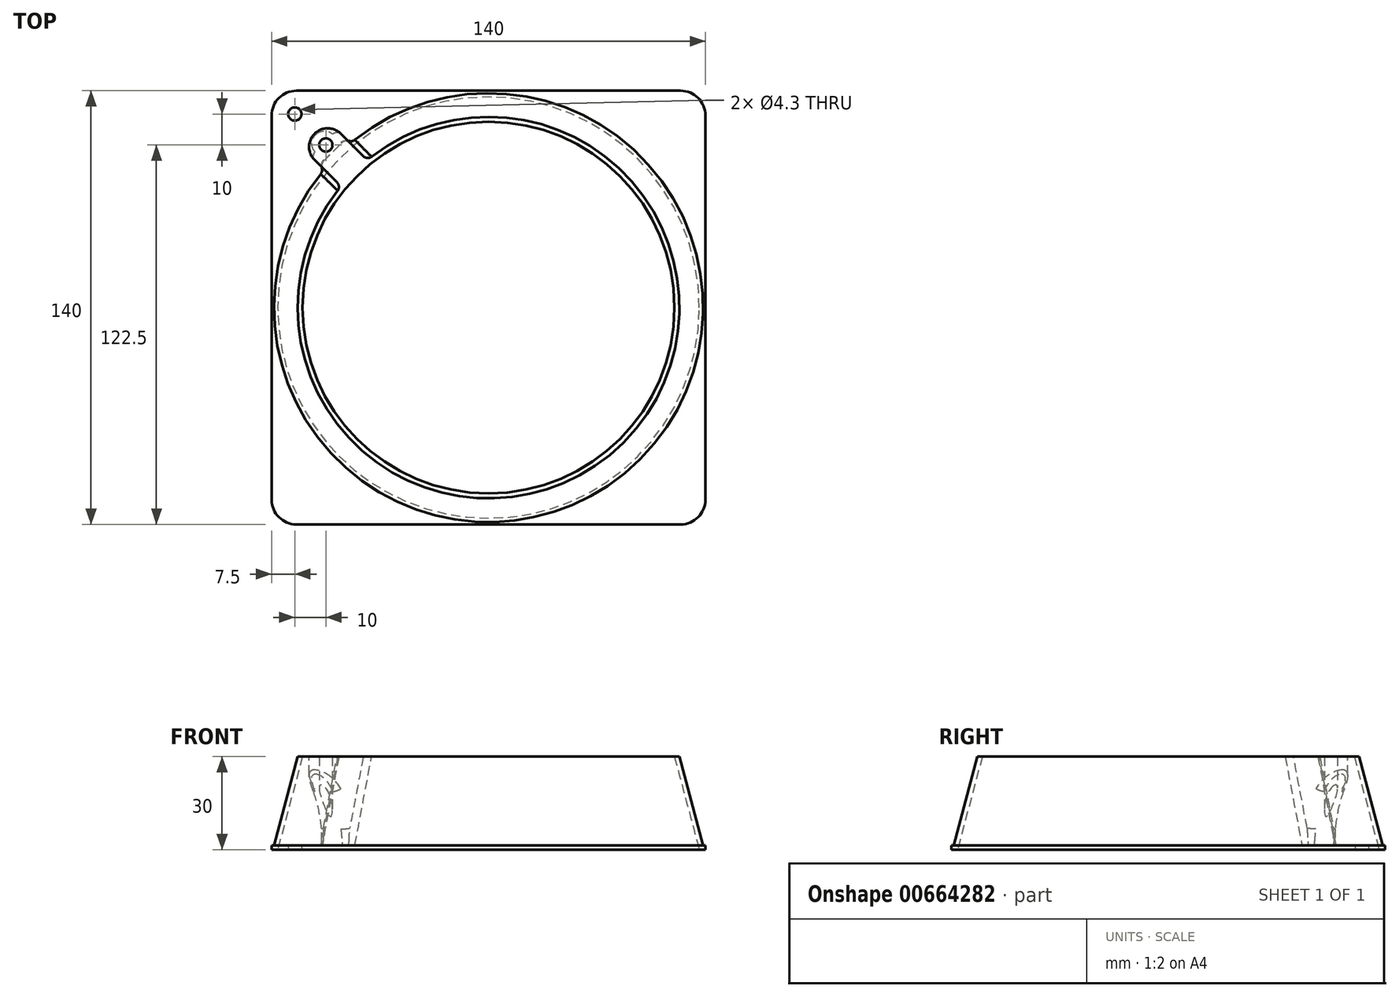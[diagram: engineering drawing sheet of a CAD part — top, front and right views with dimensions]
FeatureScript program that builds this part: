
annotation { "Feature Type Name" : "Feature", "Feature Type Description" : "" }
export const myFeature = defineFeature(function(context is Context, id is Id, definition is map)
    precondition{}
    {
        {
            var Q0;
            Q0=qCreatedBy(makeId("Top.planeOp"),FACE);
            var sketch = newSketch(context, id + "F0", { "sketchPlane" : qUnion([Q0])});
            skLineSegment(sketch, "E0.bottom", {"start": v(-70, 70) * mm, "end": v(70, 70) * mm});
            skLineSegment(sketch, "E0.top", {"start": v(-70, -70) * mm, "end": v(70, -70) * mm});
            skLineSegment(sketch, "E0.left", {"start": v(-70, 70) * mm, "end": v(-70, -70) * mm});
            skLineSegment(sketch, "E0.right", {"start": v(70, 70) * mm, "end": v(70, -70) * mm});
            skSolve(sketch);
        }
        {
            var Q0;
            Q0 = qSketchRegion(id + "F0", true);
            extrude(context, id + "F1", {"entities" : qUnion([Q0]), "depth" : 30 * mm, "offsetDistance" : 25 * mm});
        }
        {
            var Q0;
            Q0=qCreatedBy(makeId("Top.planeOp"),FACE);
            var sketch = newSketch(context, id + "F2", { "sketchPlane" : qUnion([Q0])});
            skCircle(sketch, "E1", {"center": v(-62.5, 62.5) * mm, "radius": 2.15 * mm});
            skSolve(sketch);
        }
        {
            var Q0;
            Q0=qCreatedBy(makeId("Right.planeOp"),FACE);
            var sketch = newSketch(context, id + "F3", { "sketchPlane" : qUnion([Q0])});
            skLineSegment(sketch, "E2", {"start": v(0, -23.45) * mm, "end": v(0, 54.65) * mm, "construction": true});
            skSolve(sketch);
        }
        {
            var Q0;
            Q0=qCreatedBy(makeId("Top.planeOp"),FACE);
            var sketch = newSketch(context, id + "F4", { "sketchPlane" : qUnion([Q0])});
            skCircle(sketch, "E3", {"center": v(0, 0) * mm, "radius": 68 * mm});
            skSolve(sketch);
        }
        {
            var Q0;
            Q0=makeQuery(id+"F0.imprint","IMPRINT",FACE,{"disambiguationData":[TD([[makeQuery(id+"F0.imprint","IMPRINT",EDGE,{"derivedFrom":sQuery(id+"F0.wireOp",EDGE,"E0.bottom")}),-1.0]])]});
            var sketch = newSketch(context, id + "F5", { "sketchPlane" : qUnion([Q0])});
            skCircle(sketch, "E4", {"center": v(0, 0) * mm, "radius": 69.6 * mm});
            skLineSegment(sketch, "E5.bottom", {"start": v(-83.67, 77.05) * mm, "end": v(82.18, 77.05) * mm});
            skLineSegment(sketch, "E5.top", {"start": v(-83.67, -76.06) * mm, "end": v(82.18, -76.06) * mm});
            skLineSegment(sketch, "E5.left", {"start": v(-83.67, 77.05) * mm, "end": v(-83.67, -76.06) * mm});
            skLineSegment(sketch, "E5.right", {"start": v(82.18, 77.05) * mm, "end": v(82.18, -76.06) * mm});
            skSolve(sketch);
        }
        {
            var Q0;
            Q0 = qSketchRegion(id + "F5", true);
            extrude(context, id + "F6", {"entities" : qUnion([Q0]), "operationType" : NewBodyOperationType.REMOVE, "depth" : 30 * mm, "offsetDistance" : 25 * mm, "hasDraft" : true, "draftAngle" : 14.93 * degree, "hasSecondDirection" : true, "secondDirectionOppositeDirection" : false, "secondDirectionDepth" : 1.4 * mm});
        }
        {
            var Q0;
            Q0=qCreatedBy(makeId("Top.planeOp"),FACE);
            var sketch = newSketch(context, id + "F7", { "sketchPlane" : qUnion([Q0])});
            skCircle(sketch, "E6", {"center": v(-52.5, 52.5) * mm, "radius": 2.15 * mm});
            skSolve(sketch);
        }
        {
            var Q0;
            Q0=makeQuery(id+"F0.imprint","IMPRINT",FACE,{"disambiguationData":[TD([[makeQuery(id+"F0.imprint","IMPRINT",EDGE,{"derivedFrom":sQuery(id+"F0.wireOp",EDGE,"E0.bottom")}),-1.0]])]});
            var sketch = newSketch(context, id + "F8", { "sketchPlane" : qUnion([Q0])});
            skLineSegment(sketch, "E7", {"start": v(-45.5, 37.02) * mm, "end": v(-37.02, 45.5) * mm});
            skLineSegment(sketch, "E8", {"start": v(0, 0) * mm, "end": v(-70, 70) * mm, "construction": true});
            skLineSegment(sketch, "E9", {"start": v(-45.5, 37.02) * mm, "end": v(-60.38, 51.9) * mm});
            skLineSegment(sketch, "E10", {"start": v(-37.02, 45.5) * mm, "end": v(-51.9, 60.38) * mm});
            skLineSegment(sketch, "E11", {"start": v(-60.38, 51.9) * mm, "end": v(-51.9, 60.38) * mm});
            skSolve(sketch);
        }
        {
            var Q0;
            Q0 = qSketchRegion(id + "F8", true);
            extrude(context, id + "F9", {"entities" : qUnion([Q0]), "operationType" : NewBodyOperationType.ADD, "depth" : 30 * mm, "offsetDistance" : 25 * mm});
        }
        {
            var Q0;
            Q0 = qSketchRegion(id + "F2", true);
            extrude(context, id + "F10", {"entities" : qUnion([Q0]), "operationType" : NewBodyOperationType.REMOVE, "depth" : 5 * mm, "offsetDistance" : 25 * mm});
        }
        {
            var Q0;
            Q0 = qSketchRegion(id + "F4", true);
            extrude(context, id + "F11", {"entities" : qUnion([Q0]), "operationType" : NewBodyOperationType.REMOVE, "depth" : 30 * mm, "offsetDistance" : 25 * mm, "hasDraft" : true, "draftAngle" : 14.93 * degree, "draftPullDirection" : true});
        }
        {
            var Q0;
            Q0=makeQuery(id+"F9.boolean.opBoolean","MERGE",EDGE,{"derivedFrom":[makeQuery(id+"F1.opExtrude","SWEPT_EDGE",EDGE,{"disambiguationData":[OSD([sQuery(id+"F0.wireOp",EDGE,"E0.bottom"),sQuery(id+"F0.wireOp",EDGE,"E0.left")])]}),makeQuery(id+"F9.opExtrude","SWEPT_EDGE",EDGE,{"disambiguationData":[OSD([sQuery(id+"F8.wireOp",EDGE,"bcqxiliO-g36q-Js58-HRms-isVHzeuhr4qR"),sQuery(id+"F8.wireOp",EDGE,"sepJio0f-Bdl7-0CLp-PTzf-5zJ3YjW6fdva")])]})]});
            var Q1;
            Q1=makeQuery(id+"FmQ22TMhTTGu5hA_1.3.F9.boolean.opBoolean","MERGE",EDGE,{"derivedFrom":[makeQuery(id+"F1.opExtrude","SWEPT_EDGE",EDGE,{"disambiguationData":[OSD([sQuery(id+"F0.wireOp",EDGE,"E0.bottom"),sQuery(id+"F0.wireOp",EDGE,"E0.right")])]}),makeQuery(id+"FmQ22TMhTTGu5hA_1.3.F9.opExtrude","SWEPT_EDGE",EDGE,{"disambiguationData":[OSD([sQuery(id+"F8.wireOp",EDGE,"bcqxiliO-g36q-Js58-HRms-isVHzeuhr4qR"),sQuery(id+"F8.wireOp",EDGE,"sepJio0f-Bdl7-0CLp-PTzf-5zJ3YjW6fdva")])]})]});
            var Q2;
            Q2=makeQuery(id+"FmQ22TMhTTGu5hA_1.2.F9.boolean.opBoolean","MERGE",EDGE,{"derivedFrom":[makeQuery(id+"F1.opExtrude","SWEPT_EDGE",EDGE,{"disambiguationData":[OSD([sQuery(id+"F0.wireOp",EDGE,"E0.top"),sQuery(id+"F0.wireOp",EDGE,"E0.right")])]}),makeQuery(id+"FmQ22TMhTTGu5hA_1.2.F9.opExtrude","SWEPT_EDGE",EDGE,{"disambiguationData":[OSD([sQuery(id+"F8.wireOp",EDGE,"bcqxiliO-g36q-Js58-HRms-isVHzeuhr4qR"),sQuery(id+"F8.wireOp",EDGE,"sepJio0f-Bdl7-0CLp-PTzf-5zJ3YjW6fdva")])]})]});
            var Q3;
            Q3=makeQuery(id+"FmQ22TMhTTGu5hA_1.1.F9.boolean.opBoolean","MERGE",EDGE,{"derivedFrom":[makeQuery(id+"F1.opExtrude","SWEPT_EDGE",EDGE,{"disambiguationData":[OSD([sQuery(id+"F0.wireOp",EDGE,"E0.top"),sQuery(id+"F0.wireOp",EDGE,"E0.left")])]}),makeQuery(id+"FmQ22TMhTTGu5hA_1.1.F9.opExtrude","SWEPT_EDGE",EDGE,{"disambiguationData":[OSD([sQuery(id+"F8.wireOp",EDGE,"bcqxiliO-g36q-Js58-HRms-isVHzeuhr4qR"),sQuery(id+"F8.wireOp",EDGE,"sepJio0f-Bdl7-0CLp-PTzf-5zJ3YjW6fdva")])]})]});
            fillet(context, id + "F12", {"entities" : qUnion([Q0, Q1, Q2, Q3]), "radius" : 8 * mm, "tangentPropagation" : true, "allowEdgeOverflow" : false});
        }
        {
            var Q0;
            Q0 = qSketchRegion(id + "F7", true);
            extrude(context, id + "F13", {"entities" : qUnion([Q0]), "operationType" : NewBodyOperationType.REMOVE, "depth" : 30 * mm, "offsetDistance" : 25 * mm, "hasSecondDirection" : true, "secondDirectionOppositeDirection" : false, "secondDirectionDepth" : 10 * mm});
        }
        {
            var Q0;
            Q0=qCreatedBy(makeId("Top.planeOp"),FACE);
            var sketch = newSketch(context, id + "F14", { "sketchPlane" : qUnion([Q0])});
            skLineSegment(sketch, "E12", {"start": v(-54.87, 45.68) * mm, "end": v(-62.15, 52.96) * mm});
            skLineSegment(sketch, "E13", {"start": v(-62.15, 52.96) * mm, "end": v(-52.96, 62.15) * mm});
            skLineSegment(sketch, "E14", {"start": v(-52.96, 62.15) * mm, "end": v(-45.68, 54.87) * mm});
            skLineSegment(sketch, "E15", {"start": v(-54.87, 45.68) * mm, "end": v(-45.68, 54.87) * mm});
            skSolve(sketch);
        }
        {
            var Q0;
            Q0 = qSketchRegion(id + "F14", true);
            extrude(context, id + "F15", {"entities" : qUnion([Q0]), "operationType" : NewBodyOperationType.REMOVE, "depth" : 25 * mm, "offsetDistance" : 25 * mm, "hasSecondDirection" : true, "secondDirectionOppositeDirection" : false, "secondDirectionDepth" : 1.4 * mm});
        }
        {
            var Q0;
            Q0=makeQuery(id+"FmQ22TMhTTGu5hA_1.1.F9.boolean.opBoolean","INTERSECT",EDGE,{"derivedFrom":[makeQuery(id+"F6.boolean.opBoolean","COPY",FACE,{"derivedFrom":makeQuery(id+"F6.opExtrude","SWEPT_FACE",FACE,{"disambiguationData":[OSD([sQuery(id+"F5.wireOp",EDGE,"E4")])]})}),makeQuery(id+"FmQ22TMhTTGu5hA_1.1.F9.opExtrude","SWEPT_FACE",FACE,{"disambiguationData":[OSD([sQuery(id+"F8.wireOp",EDGE,"E9")])]})]});
            var Q1;
            Q1=makeQuery(id+"FmQ22TMhTTGu5hA_1.1.F9.boolean.opBoolean","INTERSECT",EDGE,{"derivedFrom":[makeQuery(id+"F6.boolean.opBoolean","COPY",FACE,{"derivedFrom":makeQuery(id+"F6.opExtrude","SWEPT_FACE",FACE,{"disambiguationData":[OSD([sQuery(id+"F5.wireOp",EDGE,"E4")])]})}),makeQuery(id+"FmQ22TMhTTGu5hA_1.1.F9.opExtrude","SWEPT_FACE",FACE,{"disambiguationData":[OSD([sQuery(id+"F8.wireOp",EDGE,"E10")])]})]});
            var Q2;
            {var subQ0=sQuery(id+"F8.wireOp",EDGE,"E10");var subQ4=sQuery(id+"F5.wireOp",EDGE,"E4");Q2=makeQuery(id+"FmQ22TMhTTGu5hA_1.2.F9.boolean.opBoolean","INTERSECT",EDGE,{"derivedFrom":[makeQuery(id+"FmQ22TMhTTGu5hA_1.1.F9.boolean.opBoolean","SPLIT",FACE,{"disambiguationData":[TD([makeQuery(id+"F9.opExtrude","SWEPT_FACE",FACE,{"disambiguationData":[OSD([subQ0])]})])],"derivedFrom":makeQuery(id+"F6.boolean.opBoolean","COPY",FACE,{"derivedFrom":makeQuery(id+"F6.opExtrude","SWEPT_FACE",FACE,{"disambiguationData":[OSD([subQ4])]})})}),makeQuery(id+"FmQ22TMhTTGu5hA_1.2.F9.opExtrude","SWEPT_FACE",FACE,{"disambiguationData":[OSD([subQ0])]})]});}
            var Q3;
            {var subQ0=sQuery(id+"F8.wireOp",EDGE,"E9");var subQ1=sQuery(id+"F8.wireOp",EDGE,"E10");var subQ4=sQuery(id+"F5.wireOp",EDGE,"E4");Q3=makeQuery(id+"FmQ22TMhTTGu5hA_1.2.F9.boolean.opBoolean","INTERSECT",EDGE,{"derivedFrom":[makeQuery(id+"FmQ22TMhTTGu5hA_1.1.F9.boolean.opBoolean","SPLIT",FACE,{"disambiguationData":[TD([makeQuery(id+"F9.opExtrude","SWEPT_FACE",FACE,{"disambiguationData":[OSD([subQ1])]})])],"derivedFrom":makeQuery(id+"F6.boolean.opBoolean","COPY",FACE,{"derivedFrom":makeQuery(id+"F6.opExtrude","SWEPT_FACE",FACE,{"disambiguationData":[OSD([subQ4])]})})}),makeQuery(id+"FmQ22TMhTTGu5hA_1.2.F9.opExtrude","SWEPT_FACE",FACE,{"disambiguationData":[OSD([subQ0])]})]});}
            var Q4;
            {var subQ0=sQuery(id+"F8.wireOp",EDGE,"E10");var subQ1=makeQuery(id+"F9.opExtrude","SWEPT_FACE",FACE,{"disambiguationData":[OSD([subQ0])]});var subQ6=sQuery(id+"F5.wireOp",EDGE,"E4");Q4=makeQuery(id+"FmQ22TMhTTGu5hA_1.3.F9.boolean.opBoolean","INTERSECT",EDGE,{"derivedFrom":[makeQuery(id+"FmQ22TMhTTGu5hA_1.2.F9.boolean.opBoolean","SPLIT",FACE,{"disambiguationData":[TD([subQ1])],"derivedFrom":makeQuery(id+"FmQ22TMhTTGu5hA_1.1.F9.boolean.opBoolean","SPLIT",FACE,{"disambiguationData":[TD([subQ1])],"derivedFrom":makeQuery(id+"F6.boolean.opBoolean","COPY",FACE,{"derivedFrom":makeQuery(id+"F6.opExtrude","SWEPT_FACE",FACE,{"disambiguationData":[OSD([subQ6])]})})})}),makeQuery(id+"FmQ22TMhTTGu5hA_1.3.F9.opExtrude","SWEPT_FACE",FACE,{"disambiguationData":[OSD([subQ0])]})]});}
            var Q5;
            {var subQ0=sQuery(id+"F8.wireOp",EDGE,"E9");var subQ1=sQuery(id+"F8.wireOp",EDGE,"E10");var subQ2=makeQuery(id+"F9.opExtrude","SWEPT_FACE",FACE,{"disambiguationData":[OSD([subQ1])]});var subQ6=sQuery(id+"F5.wireOp",EDGE,"E4");Q5=makeQuery(id+"FmQ22TMhTTGu5hA_1.3.F9.boolean.opBoolean","INTERSECT",EDGE,{"derivedFrom":[makeQuery(id+"FmQ22TMhTTGu5hA_1.2.F9.boolean.opBoolean","SPLIT",FACE,{"disambiguationData":[TD([subQ2])],"derivedFrom":makeQuery(id+"FmQ22TMhTTGu5hA_1.1.F9.boolean.opBoolean","SPLIT",FACE,{"disambiguationData":[TD([subQ2])],"derivedFrom":makeQuery(id+"F6.boolean.opBoolean","COPY",FACE,{"derivedFrom":makeQuery(id+"F6.opExtrude","SWEPT_FACE",FACE,{"disambiguationData":[OSD([subQ6])]})})})}),makeQuery(id+"FmQ22TMhTTGu5hA_1.3.F9.opExtrude","SWEPT_FACE",FACE,{"disambiguationData":[OSD([subQ0])]})]});}
            var Q6;
            Q6=makeQuery(id+"F9.boolean.opBoolean","INTERSECT",EDGE,{"derivedFrom":[makeQuery(id+"F6.boolean.opBoolean","COPY",FACE,{"derivedFrom":makeQuery(id+"F6.opExtrude","SWEPT_FACE",FACE,{"disambiguationData":[OSD([sQuery(id+"F5.wireOp",EDGE,"E4")])]})}),makeQuery(id+"F9.opExtrude","SWEPT_FACE",FACE,{"disambiguationData":[OSD([sQuery(id+"F8.wireOp",EDGE,"E10")])]})]});
            var Q7;
            Q7=makeQuery(id+"F9.boolean.opBoolean","INTERSECT",EDGE,{"derivedFrom":[makeQuery(id+"F6.boolean.opBoolean","COPY",FACE,{"derivedFrom":makeQuery(id+"F6.opExtrude","SWEPT_FACE",FACE,{"disambiguationData":[OSD([sQuery(id+"F5.wireOp",EDGE,"E4")])]})}),makeQuery(id+"F9.opExtrude","SWEPT_FACE",FACE,{"disambiguationData":[OSD([sQuery(id+"F8.wireOp",EDGE,"E9")])]})]});
            fillet(context, id + "F16", {"entities" : qUnion([Q0, Q1, Q2, Q3, Q4, Q5, Q6, Q7]), "radius" : 2 * mm, "tangentPropagation" : true, "allowEdgeOverflow" : false});
        }
        {
            var Q0;
            Q0=makeQuery(id+"FRqQuWRhVaArxQi_1.1.F15.boolean.opBoolean","COPY",EDGE,{"derivedFrom":makeQuery(id+"FRqQuWRhVaArxQi_1.1.F15.opExtrude","CAP_EDGE",EDGE,{"disambiguationData":[OSD([sQuery(id+"F14.wireOp",EDGE,"E15")])],"isStart":false})});
            var Q1;
            Q1=makeQuery(id+"FRqQuWRhVaArxQi_1.2.F15.boolean.opBoolean","COPY",EDGE,{"derivedFrom":makeQuery(id+"FRqQuWRhVaArxQi_1.2.F15.opExtrude","CAP_EDGE",EDGE,{"disambiguationData":[OSD([sQuery(id+"F14.wireOp",EDGE,"E15")])],"isStart":false})});
            var Q2;
            Q2=makeQuery(id+"FRqQuWRhVaArxQi_1.3.F15.boolean.opBoolean","COPY",EDGE,{"derivedFrom":makeQuery(id+"FRqQuWRhVaArxQi_1.3.F15.opExtrude","CAP_EDGE",EDGE,{"disambiguationData":[OSD([sQuery(id+"F14.wireOp",EDGE,"E15")])],"isStart":false})});
            var Q3;
            Q3=makeQuery(id+"F15.boolean.opBoolean","COPY",EDGE,{"derivedFrom":makeQuery(id+"F15.opExtrude","CAP_EDGE",EDGE,{"disambiguationData":[OSD([sQuery(id+"F14.wireOp",EDGE,"E15")])],"isStart":false})});
            fillet(context, id + "F17", {"entities" : qUnion([Q0, Q1, Q2, Q3]), "radius" : 35 * mm, "tangentPropagation" : true, "allowEdgeOverflow" : false});
        }
        {
            var Q0;
            Q0=makeQuery(id+"FmQ22TMhTTGu5hA_1.2.F9.opExtrude","SWEPT_EDGE",EDGE,{"disambiguationData":[OSD([sQuery(id+"F8.wireOp",EDGE,"E9"),sQuery(id+"F8.wireOp",EDGE,"E11")])]});
            var Q1;
            Q1=makeQuery(id+"FmQ22TMhTTGu5hA_1.3.F9.opExtrude","SWEPT_EDGE",EDGE,{"disambiguationData":[OSD([sQuery(id+"F8.wireOp",EDGE,"E10"),sQuery(id+"F8.wireOp",EDGE,"E11")])]});
            var Q2;
            Q2=makeQuery(id+"FmQ22TMhTTGu5hA_1.3.F9.opExtrude","SWEPT_EDGE",EDGE,{"disambiguationData":[OSD([sQuery(id+"F8.wireOp",EDGE,"E9"),sQuery(id+"F8.wireOp",EDGE,"E11")])]});
            var Q3;
            Q3=makeQuery(id+"F9.opExtrude","SWEPT_EDGE",EDGE,{"disambiguationData":[OSD([sQuery(id+"F8.wireOp",EDGE,"E10"),sQuery(id+"F8.wireOp",EDGE,"E11")])]});
            var Q4;
            Q4=makeQuery(id+"FmQ22TMhTTGu5hA_1.2.F9.opExtrude","SWEPT_EDGE",EDGE,{"disambiguationData":[OSD([sQuery(id+"F8.wireOp",EDGE,"E10"),sQuery(id+"F8.wireOp",EDGE,"E11")])]});
            var Q5;
            Q5=makeQuery(id+"FmQ22TMhTTGu5hA_1.1.F9.opExtrude","SWEPT_EDGE",EDGE,{"disambiguationData":[OSD([sQuery(id+"F8.wireOp",EDGE,"E9"),sQuery(id+"F8.wireOp",EDGE,"E11")])]});
            var Q6;
            Q6=makeQuery(id+"FmQ22TMhTTGu5hA_1.1.F9.opExtrude","SWEPT_EDGE",EDGE,{"disambiguationData":[OSD([sQuery(id+"F8.wireOp",EDGE,"E10"),sQuery(id+"F8.wireOp",EDGE,"E11")])]});
            var Q7;
            Q7=makeQuery(id+"F9.opExtrude","SWEPT_EDGE",EDGE,{"disambiguationData":[OSD([sQuery(id+"F8.wireOp",EDGE,"E9"),sQuery(id+"F8.wireOp",EDGE,"E11")])]});
            fillet(context, id + "F18", {"entities" : qUnion([Q0, Q1, Q2, Q3, Q4, Q5, Q6, Q7]), "radius" : 6 * mm, "tangentPropagation" : true, "allowEdgeOverflow" : false});
        }
        {
            var Q0;
            Q0=makeQuery(id+"F17.opFillet","BLEND_EDGE",EDGE,{"blendedFrom":[makeQuery(id+"FRqQuWRhVaArxQi_1.1.F15.boolean.opBoolean","COPY",EDGE,{"derivedFrom":makeQuery(id+"FRqQuWRhVaArxQi_1.1.F15.opExtrude","CAP_EDGE",EDGE,{"disambiguationData":[OSD([sQuery(id+"F14.wireOp",EDGE,"E15")])],"isStart":false})}),makeQuery(id+"FmQ22TMhTTGu5hA_1.1.F9.opExtrude","SWEPT_FACE",FACE,{"disambiguationData":[OSD([sQuery(id+"F8.wireOp",EDGE,"E9")])]})],"blendedInto":[makeQuery(id+"FmQ22TMhTTGu5hA_1.1.F9.opExtrude","SWEPT_FACE",FACE,{"disambiguationData":[OSD([sQuery(id+"F8.wireOp",EDGE,"E9")])]})]});
            var Q1;
            Q1=makeQuery(id+"F17.opFillet","BLEND_EDGE",EDGE,{"blendedFrom":[makeQuery(id+"FRqQuWRhVaArxQi_1.2.F15.boolean.opBoolean","COPY",EDGE,{"derivedFrom":makeQuery(id+"FRqQuWRhVaArxQi_1.2.F15.opExtrude","CAP_EDGE",EDGE,{"disambiguationData":[OSD([sQuery(id+"F14.wireOp",EDGE,"E15")])],"isStart":false})}),makeQuery(id+"FmQ22TMhTTGu5hA_1.2.F9.opExtrude","SWEPT_FACE",FACE,{"disambiguationData":[OSD([sQuery(id+"F8.wireOp",EDGE,"E9")])]})],"blendedInto":[makeQuery(id+"FmQ22TMhTTGu5hA_1.2.F9.opExtrude","SWEPT_FACE",FACE,{"disambiguationData":[OSD([sQuery(id+"F8.wireOp",EDGE,"E9")])]})]});
            var Q2;
            Q2=makeQuery(id+"F17.opFillet","BLEND_EDGE",EDGE,{"blendedFrom":[makeQuery(id+"FRqQuWRhVaArxQi_1.3.F15.boolean.opBoolean","COPY",EDGE,{"derivedFrom":makeQuery(id+"FRqQuWRhVaArxQi_1.3.F15.opExtrude","CAP_EDGE",EDGE,{"disambiguationData":[OSD([sQuery(id+"F14.wireOp",EDGE,"E15")])],"isStart":false})}),makeQuery(id+"FmQ22TMhTTGu5hA_1.3.F9.opExtrude","SWEPT_FACE",FACE,{"disambiguationData":[OSD([sQuery(id+"F8.wireOp",EDGE,"E9")])]})],"blendedInto":[makeQuery(id+"FmQ22TMhTTGu5hA_1.3.F9.opExtrude","SWEPT_FACE",FACE,{"disambiguationData":[OSD([sQuery(id+"F8.wireOp",EDGE,"E9")])]})]});
            var Q3;
            Q3=makeQuery(id+"F17.opFillet","BLEND_EDGE",EDGE,{"blendedFrom":[makeQuery(id+"F15.boolean.opBoolean","COPY",EDGE,{"derivedFrom":makeQuery(id+"F15.opExtrude","CAP_EDGE",EDGE,{"disambiguationData":[OSD([sQuery(id+"F14.wireOp",EDGE,"E15")])],"isStart":false})}),makeQuery(id+"F9.opExtrude","SWEPT_FACE",FACE,{"disambiguationData":[OSD([sQuery(id+"F8.wireOp",EDGE,"E9")])]})],"blendedInto":[makeQuery(id+"F9.opExtrude","SWEPT_FACE",FACE,{"disambiguationData":[OSD([sQuery(id+"F8.wireOp",EDGE,"E9")])]})]});
            fillet(context, id + "F19", {"entities" : qUnion([Q0, Q1, Q2, Q3]), "radius" : 2 * mm, "tangentPropagation" : true, "allowEdgeOverflow" : false});
        }
    });
